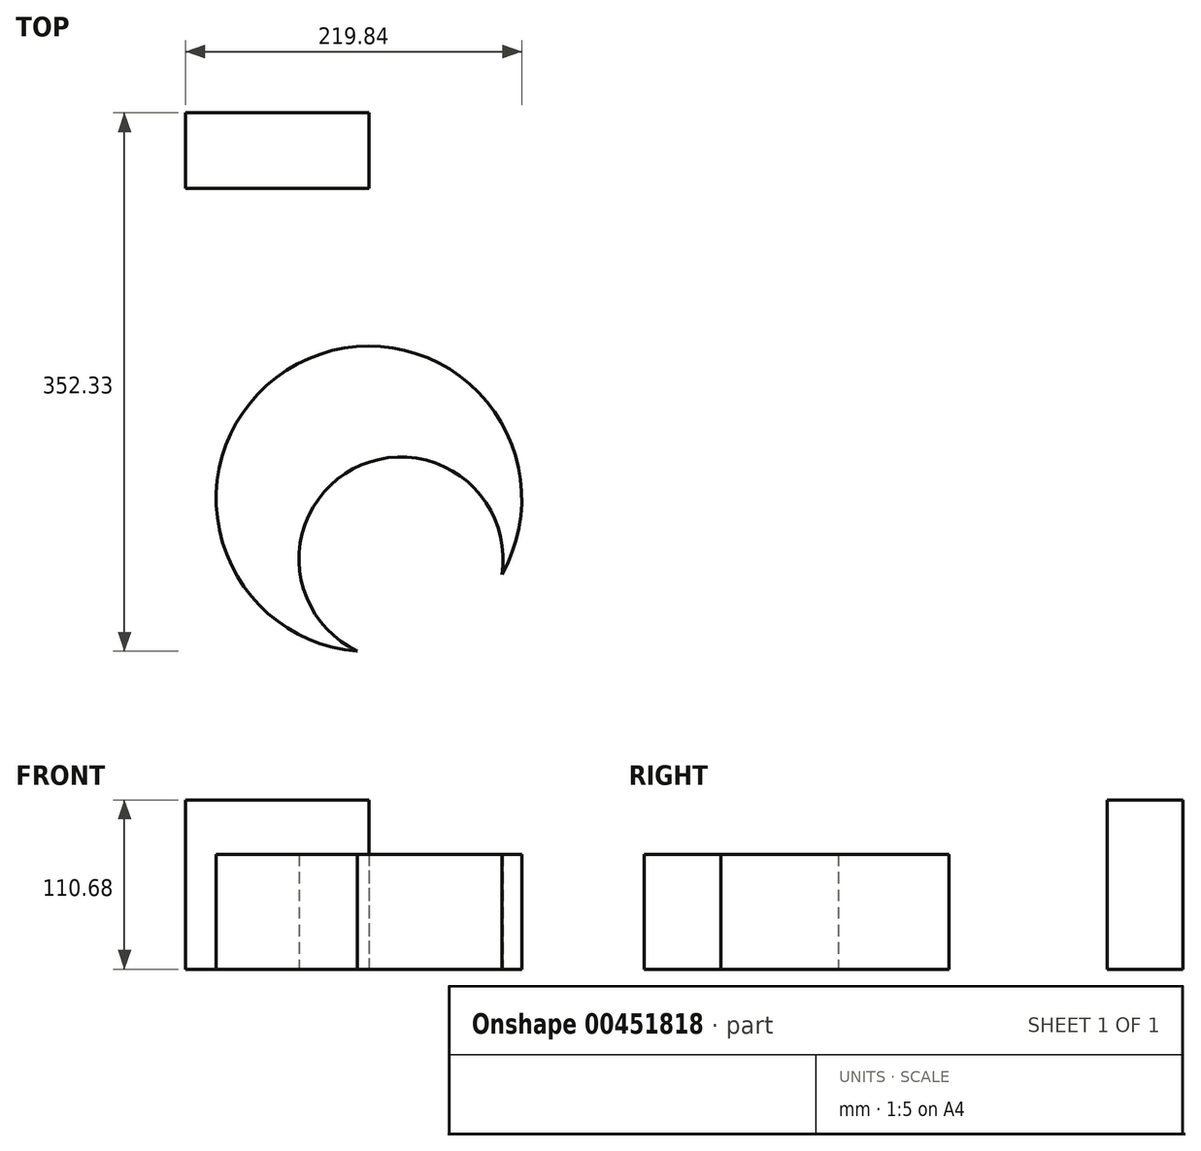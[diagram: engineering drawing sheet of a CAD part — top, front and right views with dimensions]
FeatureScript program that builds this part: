
annotation { "Feature Type Name" : "Feature", "Feature Type Description" : "" }
export const myFeature = defineFeature(function(context is Context, id is Id, definition is map)
    precondition{}
    {
        {
            var Q0;
            Q0=qCreatedBy(makeId("Front.planeOp"),FACE);
            var sketch = newSketch(context, id + "F0", { "sketchPlane" : qUnion([Q0])});
            skCircle(sketch, "E0", {"center": v(75.76, 121.12) * mm, "radius": 8.1 * mm});
            skSolve(sketch);
        }
        {
            var Q0;
            Q0=qCreatedBy(makeId("Top.planeOp"),FACE);
            var sketch = newSketch(context, id + "F1", { "sketchPlane" : qUnion([Q0])});
            skCircle(sketch, "E1", {"center": v(0, -68.86) * mm, "radius": 99.95 * mm});
            skCircle(sketch, "E2", {"center": v(20.9, -108.2) * mm, "radius": 66.72 * mm});
            skSolve(sketch);
        }
        {
            var Q0;
            Q0 = qBodyType(qCreatedBy(id + "F1" ,EDGE), BodyType.WIRE);
            var sketch = newSketch(context, id + "F2", { "sketchPlane" : qUnion([Q0])});
            skSolve(sketch);
        }
        {
            var Q0;
            Q0 = qSketchRegion(id + "F2", true);
            var Q1;
            {var subQ0=sQuery(id+"F1.wireOp",EDGE,"E2");var subQ1=sQuery(id+"F1.wireOp",EDGE,"E1");var subQ2=makeQuery(id+"F1.imprint","INTERSECT",VERTEX,{"disambiguationData":[OD(0.0)],"derivedFrom":[subQ1,subQ0]});Q1=makeQuery(id+"F1.imprint","IMPRINT",FACE,{"disambiguationData":[TD([[makeQuery(id+"F1.imprint","IMPRINT",EDGE,{"disambiguationData":[TD([[subQ2,1.0]])],"derivedFrom":subQ1}),1.0]])]});}
            extrude(context, id + "F3", {"entities" : qUnion([Q0, Q1]), "depth" : 75.08 * mm});
        }
        {
            var Q0;
            Q0=qCreatedBy(makeId("Top.planeOp"),FACE);
            var sketch = newSketch(context, id + "F4", { "sketchPlane" : qUnion([Q0])});
            skLineSegment(sketch, "E3.bottom", {"start": v(-119.89, 183.82) * mm, "end": v(0, 183.82) * mm});
            skLineSegment(sketch, "E3.top", {"start": v(-119.89, 134.3) * mm, "end": v(0, 134.3) * mm});
            skLineSegment(sketch, "E3.left", {"start": v(-119.89, 183.82) * mm, "end": v(-119.89, 134.3) * mm});
            skLineSegment(sketch, "E3.right", {"start": v(0, 183.82) * mm, "end": v(0, 134.3) * mm});
            skSolve(sketch);
        }
        {
            var Q0;
            Q0=makeQuery(id+"F4.imprint","IMPRINT",FACE,{"disambiguationData":[TD([[makeQuery(id+"F4.imprint","IMPRINT",EDGE,{"derivedFrom":sQuery(id+"F4.wireOp",EDGE,"E3.bottom")}),-1.0]])]});
            extrude(context, id + "F5", {"entities" : qUnion([Q0]), "depth" : 110.68 * mm});
        }
    });
